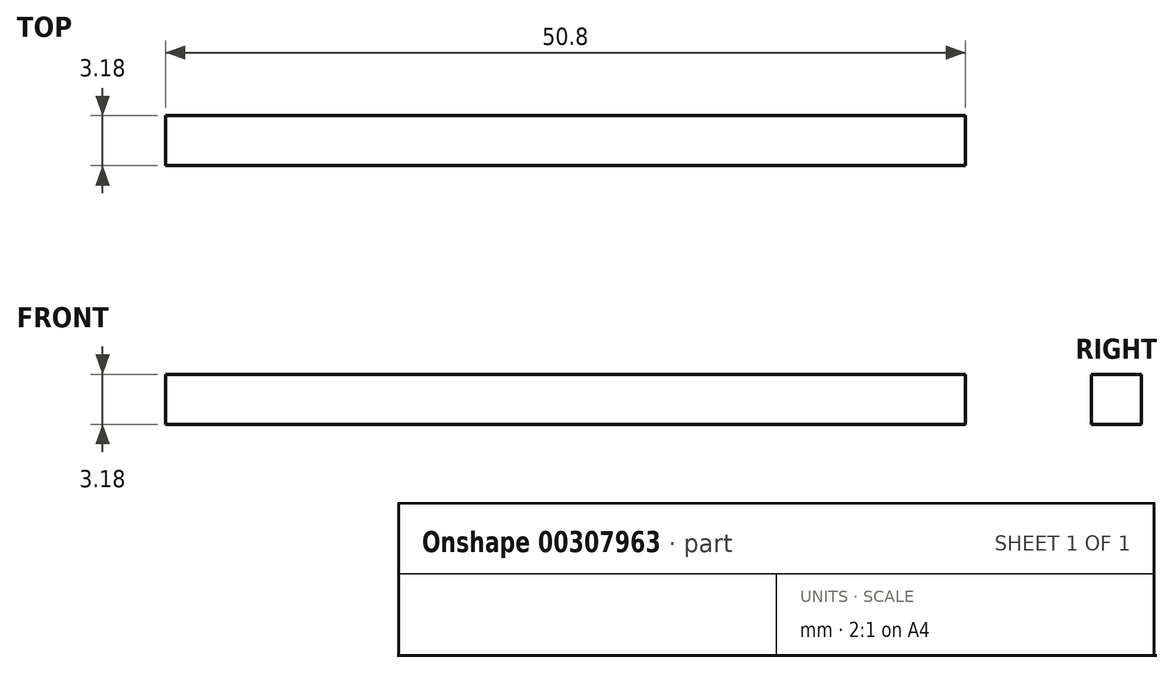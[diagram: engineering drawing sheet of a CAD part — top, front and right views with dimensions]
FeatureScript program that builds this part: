
annotation { "Feature Type Name" : "Feature", "Feature Type Description" : "" }
export const myFeature = defineFeature(function(context is Context, id is Id, definition is map)
    precondition{}
    {
        {
            var Q0;
            Q0=qCreatedBy(makeId("Front.planeOp"),FACE);
            var sketch = newSketch(context, id + "F0", { "sketchPlane" : qUnion([Q0])});
            skLineSegment(sketch, "E0.bottom", {"start": v(25.4, -1.59) * mm, "end": v(-25.4, -1.59) * mm});
            skLineSegment(sketch, "E0.top", {"start": v(25.4, 1.59) * mm, "end": v(-25.4, 1.59) * mm});
            skLineSegment(sketch, "E0.left", {"start": v(25.4, -1.59) * mm, "end": v(25.4, 1.59) * mm});
            skLineSegment(sketch, "E0.right", {"start": v(-25.4, -1.59) * mm, "end": v(-25.4, 1.59) * mm});
            skPoint(sketch, "E0.middle", {"position": v(0, 0) * mm});
            skSolve(sketch);
        }
        {
            var Q0;
            Q0=makeQuery(id+"F0.imprint","IMPRINT",FACE,{"disambiguationData":[TD([[makeQuery(id+"F0.imprint","IMPRINT",EDGE,{"derivedFrom":sQuery(id+"F0.wireOp",EDGE,"E0.bottom")}),-1.0]])]});
            extrude(context, id + "F1", {"entities" : qUnion([Q0]), "endBound" : BoundingType.SYMMETRIC, "depth" : 3.17 * mm});
        }
    });
